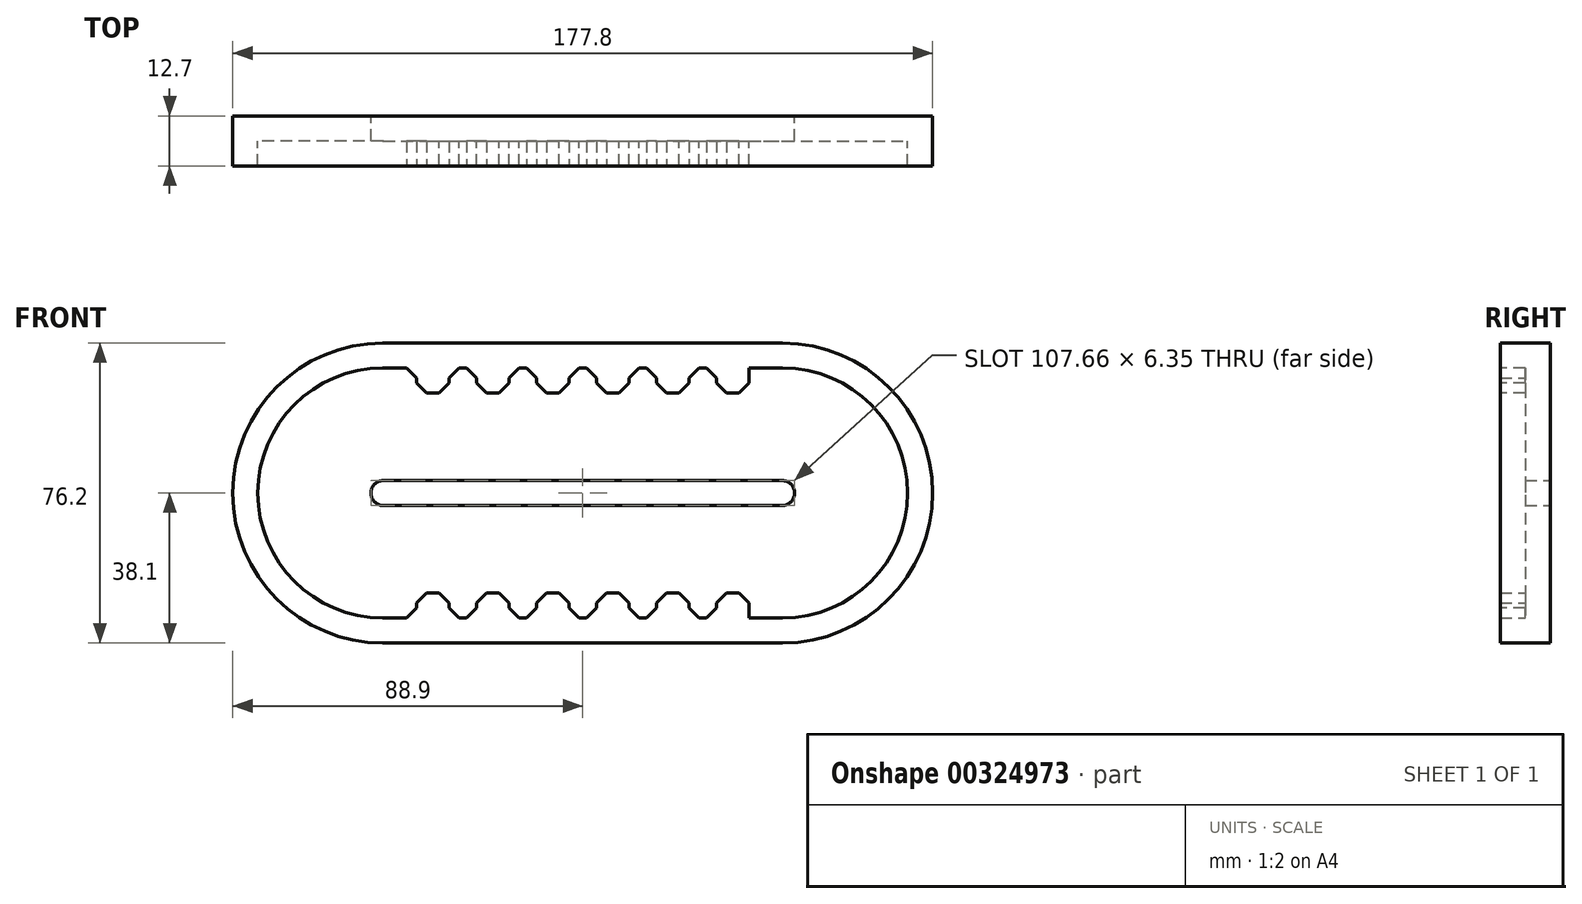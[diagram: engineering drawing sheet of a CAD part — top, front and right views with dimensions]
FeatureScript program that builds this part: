
annotation { "Feature Type Name" : "Feature", "Feature Type Description" : "" }
export const myFeature = defineFeature(function(context is Context, id is Id, definition is map)
    precondition{}
    {
        {
            var Q0;
            Q0=qCreatedBy(makeId("Front.planeOp"),FACE);
            var sketch = newSketch(context, id + "F0", { "sketchPlane" : qUnion([Q0])});
            skLineSegment(sketch, "E0", {"start": v(0, 0) * mm, "end": v(-50.8, 0) * mm, "construction": true});
            skLineSegment(sketch, "E1", {"start": v(0, 0) * mm, "end": v(50.8, 0) * mm, "construction": true});
            skLineSegment(sketch, "E2", {"start": v(-50.65, 3.18) * mm, "end": v(50.8, 3.18) * mm});
            skLineSegment(sketch, "E3", {"start": v(-50.8, 38.1) * mm, "end": v(50.8, 38.1) * mm});
            skLineSegment(sketch, "E4", {"start": v(-50.8, 31.75) * mm, "end": v(50.8, 31.75) * mm});
            skLineSegment(sketch, "E5.MirrorCS", {"start": v(-50.65, -3.18) * mm, "end": v(50.8, -3.18) * mm});
            skLineSegment(sketch, "E6.MirrorCS", {"start": v(-50.8, -38.1) * mm, "end": v(50.8, -38.1) * mm});
            skLineSegment(sketch, "E7.MirrorCS", {"start": v(-50.8, -31.75) * mm, "end": v(50.8, -31.75) * mm});
            skArc(sketch, "E8", {"start": v(-50.8, 38.1) * mm, "mid": v(-88.9, 0) * mm, "end": v(-50.8, -38.1) * mm});
            skArc(sketch, "E9", {"start": v(-50.8, 31.75) * mm, "mid": v(-82.55, 0) * mm, "end": v(-50.8, -31.75) * mm});
            skArc(sketch, "E10", {"start": v(-50.65, 3.18) * mm, "mid": v(-53.83, 0) * mm, "end": v(-50.65, -3.18) * mm});
            skArc(sketch, "E11.MirrorCS", {"start": v(50.65, 3.18) * mm, "mid": v(53.83, 0) * mm, "end": v(50.65, -3.18) * mm});
            skArc(sketch, "E12.MirrorCS", {"start": v(50.8, 38.1) * mm, "mid": v(88.9, 0) * mm, "end": v(50.8, -38.1) * mm});
            skArc(sketch, "E13.MirrorCS", {"start": v(50.8, 31.75) * mm, "mid": v(82.55, 0) * mm, "end": v(50.8, -31.75) * mm});
            skLineSegment(sketch, "E14", {"start": v(-50.8, 38.1) * mm, "end": v(-50.8, -38.1) * mm, "construction": true});
            skLineSegment(sketch, "E15", {"start": v(50.8, 38.1) * mm, "end": v(50.8, -38.1) * mm, "construction": true});
            skSolve(sketch);
        }
        {
            var Q0;
            Q0=makeQuery(id+"F0.imprint","IMPRINT",FACE,{"disambiguationData":[TD([[makeQuery(id+"F0.imprint","IMPRINT",EDGE,{"derivedFrom":sQuery(id+"F0.wireOp",EDGE,"E4")}),-1.0]])]});
            extrude(context, id + "F1", {"entities" : qUnion([Q0]), "depth" : 6.35 * mm});
        }
        {
            var Q0;
            Q0=makeQuery(id+"F0.imprint","IMPRINT",FACE,{"disambiguationData":[TD([[makeQuery(id+"F0.imprint","IMPRINT",EDGE,{"derivedFrom":sQuery(id+"F0.wireOp",EDGE,"E3")}),-1.0]])]});
            extrude(context, id + "F2", {"entities" : qUnion([Q0]), "operationType" : NewBodyOperationType.ADD, "depth" : 12.7 * mm});
        }
        {
            var Q0;
            Q0=makeQuery(id+"F1.opExtrude","CAP_FACE",FACE,{"disambiguationData":[OSD([sQuery(id+"F0.wireOp",EDGE,"E2"),sQuery(id+"F0.wireOp",EDGE,"E4"),sQuery(id+"F0.wireOp",EDGE,"E5.MirrorCS"),sQuery(id+"F0.wireOp",EDGE,"E7.MirrorCS"),sQuery(id+"F0.wireOp",EDGE,"E9"),sQuery(id+"F0.wireOp",EDGE,"E10"),sQuery(id+"F0.wireOp",EDGE,"E11.MirrorCS"),sQuery(id+"F0.wireOp",EDGE,"E13.MirrorCS")])],"isStart":false});
            var sketch = newSketch(context, id + "F3", { "sketchPlane" : qUnion([Q0])});
            skLineSegment(sketch, "E16", {"start": v(0, -31.75) * mm, "end": v(-38.1, -31.75) * mm});
            skLineSegment(sketch, "E17", {"start": v(0, -31.75) * mm, "end": v(38.1, -31.75) * mm});
            skLineSegment(sketch, "E18", {"start": v(-38.1, -25.4) * mm, "end": v(-38.1, -31.75) * mm, "construction": true});
            skLineSegment(sketch, "E19", {"start": v(38.1, -25.4) * mm, "end": v(38.1, -31.75) * mm, "construction": true});
            skLineSegment(sketch, "E20", {"start": v(-22.86, -25.4) * mm, "end": v(-22.86, -31.75) * mm, "construction": true});
            skLineSegment(sketch, "E21", {"start": v(-7.62, -25.4) * mm, "end": v(-7.62, -31.75) * mm, "construction": true});
            skLineSegment(sketch, "E22", {"start": v(7.62, -25.4) * mm, "end": v(7.62, -31.75) * mm, "construction": true});
            skLineSegment(sketch, "E23", {"start": v(22.86, -25.4) * mm, "end": v(22.86, -31.75) * mm, "construction": true});
            skLineSegment(sketch, "E24", {"start": v(-38.1, -25.4) * mm, "end": v(-42.24, -25.4) * mm});
            skLineSegment(sketch, "E25", {"start": v(-42.24, -25.4) * mm, "end": v(-33.96, -25.4) * mm});
            skLineSegment(sketch, "E26", {"start": v(-22.86, -25.4) * mm, "end": v(-27, -25.4) * mm});
            skLineSegment(sketch, "E27", {"start": v(-27, -25.4) * mm, "end": v(-18.72, -25.4) * mm});
            skLineSegment(sketch, "E28", {"start": v(-42.24, -25.4) * mm, "end": v(-42.24, -31.75) * mm});
            skLineSegment(sketch, "E29", {"start": v(-33.96, -25.4) * mm, "end": v(-33.96, -31.75) * mm});
            skLineSegment(sketch, "E30", {"start": v(-27, -25.4) * mm, "end": v(-27, -31.75) * mm});
            skLineSegment(sketch, "E31", {"start": v(-18.72, -25.4) * mm, "end": v(-18.72, -31.75) * mm});
            skLineSegment(sketch, "E32", {"start": v(-7.62, -25.4) * mm, "end": v(-11.75, -25.4) * mm});
            skLineSegment(sketch, "E33", {"start": v(-3.48, -25.4) * mm, "end": v(-7.62, -25.4) * mm});
            skLineSegment(sketch, "E34", {"start": v(-11.75, -25.4) * mm, "end": v(-11.75, -31.75) * mm});
            skLineSegment(sketch, "E35", {"start": v(-3.48, -25.4) * mm, "end": v(-3.48, -31.75) * mm});
            skLineSegment(sketch, "E36", {"start": v(7.62, -25.4) * mm, "end": v(3.48, -25.4) * mm});
            skLineSegment(sketch, "E37", {"start": v(7.62, -25.4) * mm, "end": v(11.76, -25.4) * mm});
            skLineSegment(sketch, "E38", {"start": v(11.76, -25.4) * mm, "end": v(11.76, -31.75) * mm});
            skLineSegment(sketch, "E39", {"start": v(3.48, -25.4) * mm, "end": v(3.48, -31.75) * mm});
            skLineSegment(sketch, "E40", {"start": v(22.86, -25.4) * mm, "end": v(18.72, -25.4) * mm});
            skLineSegment(sketch, "E41", {"start": v(18.72, -25.4) * mm, "end": v(18.72, -31.75) * mm});
            skLineSegment(sketch, "E42", {"start": v(22.86, -25.4) * mm, "end": v(27, -25.4) * mm});
            skLineSegment(sketch, "E43", {"start": v(27, -25.4) * mm, "end": v(27, -31.75) * mm});
            skLineSegment(sketch, "E44", {"start": v(38.1, -25.4) * mm, "end": v(33.96, -25.4) * mm});
            skLineSegment(sketch, "E45", {"start": v(33.96, -25.4) * mm, "end": v(33.96, -31.75) * mm});
            skLineSegment(sketch, "E46", {"start": v(38.1, -25.4) * mm, "end": v(42.24, -25.4) * mm});
            skLineSegment(sketch, "E47", {"start": v(42.24, -25.4) * mm, "end": v(42.24, -31.75) * mm});
            skLineSegment(sketch, "E48.MirrorCS", {"start": v(-42.24, 25.4) * mm, "end": v(-42.24, 31.75) * mm});
            skLineSegment(sketch, "E49.MirrorCS", {"start": v(-42.24, 25.4) * mm, "end": v(-33.96, 25.4) * mm});
            skLineSegment(sketch, "E50.MirrorCS", {"start": v(-33.96, 25.4) * mm, "end": v(-33.96, 31.75) * mm});
            skLineSegment(sketch, "E51.MirrorCS", {"start": v(-27, 25.4) * mm, "end": v(-27, 31.75) * mm});
            skLineSegment(sketch, "E52.MirrorCS", {"start": v(-27, 25.4) * mm, "end": v(-18.72, 25.4) * mm});
            skLineSegment(sketch, "E53.MirrorCS", {"start": v(-18.72, 25.4) * mm, "end": v(-18.72, 31.75) * mm});
            skLineSegment(sketch, "E54.MirrorCS", {"start": v(-11.75, 25.4) * mm, "end": v(-11.75, 31.75) * mm});
            skLineSegment(sketch, "E55.MirrorCS", {"start": v(-7.62, 25.4) * mm, "end": v(-11.75, 25.4) * mm});
            skLineSegment(sketch, "E56.MirrorCS", {"start": v(-3.48, 25.4) * mm, "end": v(-7.62, 25.4) * mm});
            skLineSegment(sketch, "E57.MirrorCS", {"start": v(-3.48, 25.4) * mm, "end": v(-3.48, 31.75) * mm});
            skLineSegment(sketch, "E58.MirrorCS", {"start": v(7.62, 25.4) * mm, "end": v(3.48, 25.4) * mm});
            skLineSegment(sketch, "E59.MirrorCS", {"start": v(7.62, 25.4) * mm, "end": v(11.76, 25.4) * mm});
            skLineSegment(sketch, "E60.MirrorCS", {"start": v(11.76, 25.4) * mm, "end": v(11.76, 31.75) * mm});
            skLineSegment(sketch, "E61.MirrorCS", {"start": v(3.48, 25.4) * mm, "end": v(3.48, 31.75) * mm});
            skLineSegment(sketch, "E62.MirrorCS", {"start": v(18.72, 25.4) * mm, "end": v(18.72, 31.75) * mm});
            skLineSegment(sketch, "E63.MirrorCS", {"start": v(22.86, 25.4) * mm, "end": v(18.72, 25.4) * mm});
            skLineSegment(sketch, "E64.MirrorCS", {"start": v(22.86, 25.4) * mm, "end": v(27, 25.4) * mm});
            skLineSegment(sketch, "E65.MirrorCS", {"start": v(27, 25.4) * mm, "end": v(27, 31.75) * mm});
            skLineSegment(sketch, "E66.MirrorCS", {"start": v(38.1, 25.4) * mm, "end": v(33.96, 25.4) * mm});
            skLineSegment(sketch, "E67.MirrorCS", {"start": v(38.1, 25.4) * mm, "end": v(42.24, 25.4) * mm});
            skLineSegment(sketch, "E68.MirrorCS", {"start": v(42.24, 25.4) * mm, "end": v(42.24, 31.75) * mm});
            skLineSegment(sketch, "E69.MirrorCS", {"start": v(33.96, 25.4) * mm, "end": v(33.96, 31.75) * mm});
            skSolve(sketch);
        }
        {
            var Q0;
            {var subQ0=sQuery(id+"F3.wireOp",EDGE,"E28");Q0=makeQuery(id+"F3.imprint","IMPRINT",FACE,{"disambiguationData":[TD([[makeQuery(id+"F3.imprint","IMPRINT",EDGE,{"derivedFrom":subQ0}),1.0]])]});}
            var Q1;
            {var subQ0=sQuery(id+"F3.wireOp",EDGE,"E30");Q1=makeQuery(id+"F3.imprint","IMPRINT",FACE,{"disambiguationData":[TD([[makeQuery(id+"F3.imprint","IMPRINT",EDGE,{"derivedFrom":subQ0}),1.0]])]});}
            var Q2;
            Q2=makeQuery(id+"F3.imprint","IMPRINT",FACE,{"disambiguationData":[TD([[makeQuery(id+"F3.imprint","IMPRINT",EDGE,{"derivedFrom":sQuery(id+"F3.wireOp",EDGE,"E32")}),1.0]])]});
            var Q3;
            Q3=makeQuery(id+"F3.imprint","IMPRINT",FACE,{"disambiguationData":[TD([[makeQuery(id+"F3.imprint","IMPRINT",EDGE,{"derivedFrom":sQuery(id+"F3.wireOp",EDGE,"E36")}),1.0]])]});
            var Q4;
            Q4=makeQuery(id+"F3.imprint","IMPRINT",FACE,{"disambiguationData":[TD([[makeQuery(id+"F3.imprint","IMPRINT",EDGE,{"derivedFrom":sQuery(id+"F3.wireOp",EDGE,"E40")}),1.0]])]});
            var Q5;
            {var subQ0=sQuery(id+"F3.wireOp",EDGE,"E19");Q5=makeQuery(id+"F3.imprint","IMPRINT",FACE,{"disambiguationData":[TD([[makeQuery(id+"F3.imprint","IMPRINT",EDGE,{"derivedFrom":subQ0}),1.0]])]});}
            var Q6;
            {var subQ0=sQuery(id+"F3.wireOp",EDGE,"E19");Q6=makeQuery(id+"F3.imprint","IMPRINT",FACE,{"disambiguationData":[TD([[makeQuery(id+"F3.imprint","IMPRINT",EDGE,{"derivedFrom":subQ0}),-1.0]])]});}
            var Q7;
            Q7=makeQuery(id+"F3.imprint","IMPRINT",FACE,{"disambiguationData":[TD([[makeQuery(id+"F3.imprint","IMPRINT",EDGE,{"derivedFrom":sQuery(id+"F3.wireOp",EDGE,"E44")}),1.0]])]});
            extrude(context, id + "F4", {"entities" : qUnion([Q0, Q1, Q2, Q3, Q4, Q5, Q6, Q7]), "operationType" : NewBodyOperationType.ADD, "depth" : 6.35 * mm});
        }
        {
            var Q0;
            Q0=makeQuery(id+"F4.opExtrude","SWEPT_EDGE",EDGE,{"disambiguationData":[OSD([sQuery(id+"F3.wireOp",EDGE,"E25"),sQuery(id+"F3.wireOp",EDGE,"E28")])]});
            var Q1;
            Q1=makeQuery(id+"F4.opExtrude","SWEPT_EDGE",EDGE,{"disambiguationData":[OSD([sQuery(id+"F3.wireOp",EDGE,"E25"),sQuery(id+"F3.wireOp",EDGE,"E29")])]});
            var Q2;
            Q2=makeQuery(id+"F4.opExtrude","SWEPT_EDGE",EDGE,{"disambiguationData":[OSD([sQuery(id+"F3.wireOp",EDGE,"E27"),sQuery(id+"F3.wireOp",EDGE,"E30")])]});
            var Q3;
            Q3=makeQuery(id+"F4.opExtrude","SWEPT_EDGE",EDGE,{"disambiguationData":[OSD([sQuery(id+"F3.wireOp",EDGE,"E27"),sQuery(id+"F3.wireOp",EDGE,"E31")])]});
            var Q4;
            Q4=makeQuery(id+"F4.opExtrude","SWEPT_EDGE",EDGE,{"disambiguationData":[OSD([sQuery(id+"F3.wireOp",EDGE,"E32"),sQuery(id+"F3.wireOp",EDGE,"E34")])]});
            var Q5;
            Q5=makeQuery(id+"F4.opExtrude","SWEPT_EDGE",EDGE,{"disambiguationData":[OSD([sQuery(id+"F3.wireOp",EDGE,"E33"),sQuery(id+"F3.wireOp",EDGE,"E35")])]});
            var Q6;
            Q6=makeQuery(id+"F4.opExtrude","SWEPT_EDGE",EDGE,{"disambiguationData":[OSD([sQuery(id+"F3.wireOp",EDGE,"E36"),sQuery(id+"F3.wireOp",EDGE,"E39")])]});
            var Q7;
            Q7=makeQuery(id+"F4.opExtrude","SWEPT_EDGE",EDGE,{"disambiguationData":[OSD([sQuery(id+"F3.wireOp",EDGE,"E37"),sQuery(id+"F3.wireOp",EDGE,"E38")])]});
            var Q8;
            Q8=makeQuery(id+"F4.opExtrude","SWEPT_EDGE",EDGE,{"disambiguationData":[OSD([sQuery(id+"F3.wireOp",EDGE,"E40"),sQuery(id+"F3.wireOp",EDGE,"E41")])]});
            var Q9;
            Q9=makeQuery(id+"F4.opExtrude","SWEPT_EDGE",EDGE,{"disambiguationData":[OSD([sQuery(id+"F3.wireOp",EDGE,"E42"),sQuery(id+"F3.wireOp",EDGE,"E43")])]});
            var Q10;
            Q10=makeQuery(id+"F4.opExtrude","SWEPT_EDGE",EDGE,{"disambiguationData":[OSD([sQuery(id+"F3.wireOp",EDGE,"E44"),sQuery(id+"F3.wireOp",EDGE,"E45")])]});
            var Q11;
            Q11=makeQuery(id+"F4.opExtrude","SWEPT_EDGE",EDGE,{"disambiguationData":[OSD([sQuery(id+"F3.wireOp",EDGE,"E46"),sQuery(id+"F3.wireOp",EDGE,"E47")])]});
            var Q12;
            Q12=makeQuery(id+"F4.opExtrude","SWEPT_EDGE",EDGE,{"disambiguationData":[OSD([sQuery(id+"F3.wireOp",EDGE,"E17"),sQuery(id+"F3.wireOp",EDGE,"E45")])]});
            var Q13;
            Q13=makeQuery(id+"F4.opExtrude","SWEPT_EDGE",EDGE,{"disambiguationData":[OSD([sQuery(id+"F0.wireOp",EDGE,"E7.MirrorCS"),sQuery(id+"F3.wireOp",EDGE,"E47")])]});
            var Q14;
            Q14=makeQuery(id+"F4.opExtrude","SWEPT_EDGE",EDGE,{"disambiguationData":[OSD([sQuery(id+"F3.wireOp",EDGE,"E17"),sQuery(id+"F3.wireOp",EDGE,"E43")])]});
            var Q15;
            Q15=makeQuery(id+"F4.opExtrude","SWEPT_EDGE",EDGE,{"disambiguationData":[OSD([sQuery(id+"F3.wireOp",EDGE,"E17"),sQuery(id+"F3.wireOp",EDGE,"E38")])]});
            var Q16;
            Q16=makeQuery(id+"F4.opExtrude","SWEPT_EDGE",EDGE,{"disambiguationData":[OSD([sQuery(id+"F3.wireOp",EDGE,"E17"),sQuery(id+"F3.wireOp",EDGE,"E41")])]});
            var Q17;
            Q17=makeQuery(id+"F4.opExtrude","SWEPT_EDGE",EDGE,{"disambiguationData":[OSD([sQuery(id+"F3.wireOp",EDGE,"E17"),sQuery(id+"F3.wireOp",EDGE,"E39")])]});
            var Q18;
            Q18=makeQuery(id+"F4.opExtrude","SWEPT_EDGE",EDGE,{"disambiguationData":[OSD([sQuery(id+"F3.wireOp",EDGE,"E16"),sQuery(id+"F3.wireOp",EDGE,"E34")])]});
            var Q19;
            Q19=makeQuery(id+"F4.opExtrude","SWEPT_EDGE",EDGE,{"disambiguationData":[OSD([sQuery(id+"F3.wireOp",EDGE,"E16"),sQuery(id+"F3.wireOp",EDGE,"E30")])]});
            var Q20;
            Q20=makeQuery(id+"F4.opExtrude","SWEPT_EDGE",EDGE,{"disambiguationData":[OSD([sQuery(id+"F3.wireOp",EDGE,"E16"),sQuery(id+"F3.wireOp",EDGE,"E35")])]});
            var Q21;
            Q21=makeQuery(id+"F4.opExtrude","SWEPT_EDGE",EDGE,{"disambiguationData":[OSD([sQuery(id+"F3.wireOp",EDGE,"E16"),sQuery(id+"F3.wireOp",EDGE,"E31")])]});
            var Q22;
            Q22=makeQuery(id+"F4.opExtrude","SWEPT_EDGE",EDGE,{"disambiguationData":[OSD([sQuery(id+"F3.wireOp",EDGE,"E16"),sQuery(id+"F3.wireOp",EDGE,"E29")])]});
            var Q23;
            Q23=makeQuery(id+"F4.opExtrude","SWEPT_EDGE",EDGE,{"disambiguationData":[OSD([sQuery(id+"F0.wireOp",EDGE,"E7.MirrorCS"),sQuery(id+"F3.wireOp",EDGE,"E28")])]});
            chamfer(context, id + "F5", {"entities" : qUnion([Q0, Q1, Q2, Q3, Q4, Q5, Q6, Q7, Q8, Q9, Q10, Q11, Q12, Q13, Q14, Q15, Q16, Q17, Q18, Q19, Q20, Q21, Q22, Q23]), "width" : 2.54 * mm, "tangentPropagation" : true});
        }
        {
            var Q0;
            {var subQ0=sQuery(id+"F3.wireOp",EDGE,"E48.MirrorCS");Q0=makeQuery(id+"F3.imprint","IMPRINT",FACE,{"disambiguationData":[TD([[makeQuery(id+"F3.imprint","IMPRINT",EDGE,{"derivedFrom":subQ0}),-1.0]])]});}
            var Q1;
            {var subQ0=sQuery(id+"F3.wireOp",EDGE,"E51.MirrorCS");Q1=makeQuery(id+"F3.imprint","IMPRINT",FACE,{"disambiguationData":[TD([[makeQuery(id+"F3.imprint","IMPRINT",EDGE,{"derivedFrom":subQ0}),-1.0]])]});}
            var Q2;
            {var subQ1=sQuery(id+"F3.wireOp",EDGE,"E54.MirrorCS");Q2=makeQuery(id+"F3.imprint","IMPRINT",FACE,{"disambiguationData":[TD([[makeQuery(id+"F3.imprint","IMPRINT",EDGE,{"derivedFrom":subQ1}),-1.0]])]});}
            var Q3;
            Q3=makeQuery(id+"F3.imprint","IMPRINT",FACE,{"disambiguationData":[TD([[makeQuery(id+"F3.imprint","IMPRINT",EDGE,{"derivedFrom":sQuery(id+"F3.wireOp",EDGE,"E58.MirrorCS")}),-1.0]])]});
            var Q4;
            {var subQ1=sQuery(id+"F3.wireOp",EDGE,"E62.MirrorCS");Q4=makeQuery(id+"F3.imprint","IMPRINT",FACE,{"disambiguationData":[TD([[makeQuery(id+"F3.imprint","IMPRINT",EDGE,{"derivedFrom":subQ1}),-1.0]])]});}
            var Q5;
            Q5=makeQuery(id+"F3.imprint","IMPRINT",FACE,{"disambiguationData":[TD([[makeQuery(id+"F3.imprint","IMPRINT",EDGE,{"derivedFrom":sQuery(id+"F3.wireOp",EDGE,"E66.MirrorCS")}),-1.0]])]});
            extrude(context, id + "F6", {"entities" : qUnion([Q0, Q1, Q2, Q3, Q4, Q5]), "operationType" : NewBodyOperationType.ADD, "depth" : 6.35 * mm});
        }
        {
            var Q0;
            Q0=makeQuery(id+"F6.opExtrude","SWEPT_EDGE",EDGE,{"disambiguationData":[OSD([sQuery(id+"F0.wireOp",EDGE,"E4"),sQuery(id+"F3.wireOp",EDGE,"E48.MirrorCS")])]});
            var Q1;
            Q1=makeQuery(id+"F6.opExtrude","SWEPT_EDGE",EDGE,{"disambiguationData":[OSD([sQuery(id+"F0.wireOp",EDGE,"E4"),sQuery(id+"F3.wireOp",EDGE,"E51.MirrorCS")])]});
            var Q2;
            Q2=makeQuery(id+"F6.opExtrude","SWEPT_EDGE",EDGE,{"disambiguationData":[OSD([sQuery(id+"F3.wireOp",EDGE,"E48.MirrorCS"),sQuery(id+"F3.wireOp",EDGE,"E49.MirrorCS")])]});
            var Q3;
            Q3=makeQuery(id+"F6.opExtrude","SWEPT_EDGE",EDGE,{"disambiguationData":[OSD([sQuery(id+"F3.wireOp",EDGE,"E49.MirrorCS"),sQuery(id+"F3.wireOp",EDGE,"E50.MirrorCS")])]});
            var Q4;
            Q4=makeQuery(id+"F6.opExtrude","SWEPT_EDGE",EDGE,{"disambiguationData":[OSD([sQuery(id+"F0.wireOp",EDGE,"E4"),sQuery(id+"F3.wireOp",EDGE,"E50.MirrorCS")])]});
            var Q5;
            Q5=makeQuery(id+"F6.opExtrude","SWEPT_EDGE",EDGE,{"disambiguationData":[OSD([sQuery(id+"F3.wireOp",EDGE,"E51.MirrorCS"),sQuery(id+"F3.wireOp",EDGE,"E52.MirrorCS")])]});
            var Q6;
            Q6=makeQuery(id+"F6.opExtrude","SWEPT_EDGE",EDGE,{"disambiguationData":[OSD([sQuery(id+"F3.wireOp",EDGE,"E52.MirrorCS"),sQuery(id+"F3.wireOp",EDGE,"E53.MirrorCS")])]});
            var Q7;
            Q7=makeQuery(id+"F6.opExtrude","SWEPT_EDGE",EDGE,{"disambiguationData":[OSD([sQuery(id+"F0.wireOp",EDGE,"E4"),sQuery(id+"F3.wireOp",EDGE,"E53.MirrorCS")])]});
            var Q8;
            Q8=makeQuery(id+"F6.opExtrude","SWEPT_EDGE",EDGE,{"disambiguationData":[OSD([sQuery(id+"F3.wireOp",EDGE,"E54.MirrorCS"),sQuery(id+"F3.wireOp",EDGE,"E55.MirrorCS")])]});
            var Q9;
            Q9=makeQuery(id+"F6.opExtrude","SWEPT_EDGE",EDGE,{"disambiguationData":[OSD([sQuery(id+"F0.wireOp",EDGE,"E4"),sQuery(id+"F3.wireOp",EDGE,"E54.MirrorCS")])]});
            var Q10;
            Q10=makeQuery(id+"F6.opExtrude","SWEPT_EDGE",EDGE,{"disambiguationData":[OSD([sQuery(id+"F3.wireOp",EDGE,"E56.MirrorCS"),sQuery(id+"F3.wireOp",EDGE,"E57.MirrorCS")])]});
            var Q11;
            Q11=makeQuery(id+"F6.opExtrude","SWEPT_EDGE",EDGE,{"disambiguationData":[OSD([sQuery(id+"F3.wireOp",EDGE,"E58.MirrorCS"),sQuery(id+"F3.wireOp",EDGE,"E61.MirrorCS")])]});
            var Q12;
            Q12=makeQuery(id+"F6.opExtrude","SWEPT_EDGE",EDGE,{"disambiguationData":[OSD([sQuery(id+"F3.wireOp",EDGE,"E59.MirrorCS"),sQuery(id+"F3.wireOp",EDGE,"E60.MirrorCS")])]});
            var Q13;
            Q13=makeQuery(id+"F6.opExtrude","SWEPT_EDGE",EDGE,{"disambiguationData":[OSD([sQuery(id+"F3.wireOp",EDGE,"E62.MirrorCS"),sQuery(id+"F3.wireOp",EDGE,"E63.MirrorCS")])]});
            var Q14;
            Q14=makeQuery(id+"F6.opExtrude","SWEPT_EDGE",EDGE,{"disambiguationData":[OSD([sQuery(id+"F3.wireOp",EDGE,"E64.MirrorCS"),sQuery(id+"F3.wireOp",EDGE,"E65.MirrorCS")])]});
            var Q15;
            Q15=makeQuery(id+"F6.opExtrude","SWEPT_EDGE",EDGE,{"disambiguationData":[OSD([sQuery(id+"F3.wireOp",EDGE,"E66.MirrorCS"),sQuery(id+"F3.wireOp",EDGE,"E69.MirrorCS")])]});
            var Q16;
            Q16=makeQuery(id+"F6.opExtrude","SWEPT_EDGE",EDGE,{"disambiguationData":[OSD([sQuery(id+"F3.wireOp",EDGE,"E67.MirrorCS"),sQuery(id+"F3.wireOp",EDGE,"E68.MirrorCS")])]});
            var Q17;
            Q17=makeQuery(id+"F6.opExtrude","SWEPT_EDGE",EDGE,{"disambiguationData":[OSD([sQuery(id+"F0.wireOp",EDGE,"E4"),sQuery(id+"F3.wireOp",EDGE,"E68.MirrorCS")])]});
            var Q18;
            Q18=makeQuery(id+"F6.opExtrude","SWEPT_EDGE",EDGE,{"disambiguationData":[OSD([sQuery(id+"F0.wireOp",EDGE,"E4"),sQuery(id+"F3.wireOp",EDGE,"E65.MirrorCS")])]});
            var Q19;
            Q19=makeQuery(id+"F6.opExtrude","SWEPT_EDGE",EDGE,{"disambiguationData":[OSD([sQuery(id+"F0.wireOp",EDGE,"E4"),sQuery(id+"F3.wireOp",EDGE,"E60.MirrorCS")])]});
            var Q20;
            Q20=makeQuery(id+"F6.opExtrude","SWEPT_EDGE",EDGE,{"disambiguationData":[OSD([sQuery(id+"F0.wireOp",EDGE,"E4"),sQuery(id+"F3.wireOp",EDGE,"E62.MirrorCS")])]});
            var Q21;
            Q21=makeQuery(id+"F6.opExtrude","SWEPT_EDGE",EDGE,{"disambiguationData":[OSD([sQuery(id+"F0.wireOp",EDGE,"E4"),sQuery(id+"F3.wireOp",EDGE,"E69.MirrorCS")])]});
            var Q22;
            Q22=makeQuery(id+"F6.opExtrude","SWEPT_EDGE",EDGE,{"disambiguationData":[OSD([sQuery(id+"F0.wireOp",EDGE,"E4"),sQuery(id+"F3.wireOp",EDGE,"E57.MirrorCS")])]});
            var Q23;
            Q23=makeQuery(id+"F6.opExtrude","SWEPT_EDGE",EDGE,{"disambiguationData":[OSD([sQuery(id+"F0.wireOp",EDGE,"E4"),sQuery(id+"F3.wireOp",EDGE,"E61.MirrorCS")])]});
            chamfer(context, id + "F7", {"entities" : qUnion([Q0, Q1, Q2, Q3, Q4, Q5, Q6, Q7, Q8, Q9, Q10, Q11, Q12, Q13, Q14, Q15, Q16, Q17, Q18, Q19, Q20, Q21, Q22, Q23]), "width" : 2.54 * mm, "tangentPropagation" : true});
        }
    });
